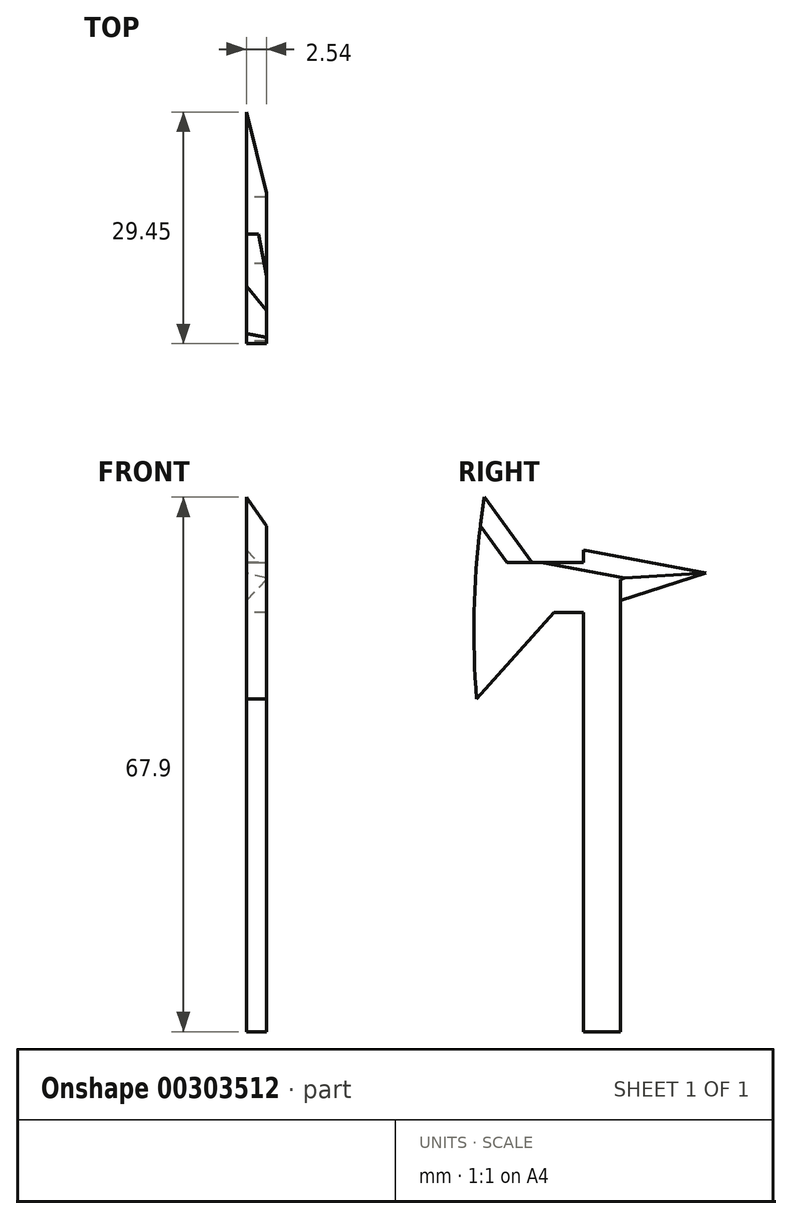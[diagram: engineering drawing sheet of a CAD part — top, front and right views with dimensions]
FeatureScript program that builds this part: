
annotation { "Feature Type Name" : "Feature", "Feature Type Description" : "" }
export const myFeature = defineFeature(function(context is Context, id is Id, definition is map)
    precondition{}
    {
        {
            var Q0;
            Q0=qCreatedBy(makeId("Right.planeOp"),FACE);
            var sketch = newSketch(context, id + "F0", { "sketchPlane" : qUnion([Q0])});
            skLineSegment(sketch, "E0", {"start": v(-4.7, 0) * mm, "end": v(-4.7, -62.89) * mm});
            skLineSegment(sketch, "E1", {"start": v(-4.7, -62.89) * mm, "end": v(0, -62.89) * mm});
            skLineSegment(sketch, "E2", {"start": v(-4.7, 0) * mm, "end": v(0, 0) * mm});
            skPoint(sketch, "E3.endSnap0", {"position": v(-2.35, 0) * mm});
            skLineSegment(sketch, "E4", {"start": v(0, 0) * mm, "end": v(21.16, -4) * mm});
            skLineSegment(sketch, "E5", {"start": v(0, -10.77) * mm, "end": v(21.16, -4) * mm});
            skLineSegment(sketch, "E6", {"start": v(-4.7, -3.27) * mm, "end": v(-8.13, -3.27) * mm});
            skLineSegment(sketch, "E7", {"start": v(-8.13, -3.27) * mm, "end": v(-16.72, 8.5) * mm});
            skLineSegment(sketch, "E8", {"start": v(-18.28, -20.64) * mm, "end": v(-8.44, -9.64) * mm});
            skLineSegment(sketch, "E9", {"start": v(-8.44, -9.64) * mm, "end": v(-4.7, -9.64) * mm});
            skArc(sketch, "E10", {"start": v(-16.72, 8.5) * mm, "mid": v(-18.45, -6.02) * mm, "end": v(-18.28, -20.64) * mm});
            skLineSegment(sketch, "E11", {"start": v(-0.3, 0) * mm, "end": v(0, -10.77) * mm});
            skLineSegment(sketch, "E12", {"start": v(0, -10.77) * mm, "end": v(0, -62.89) * mm});
            skSolve(sketch);
        }
        {
            var Q0;
            Q0 = qSketchRegion(id + "F0", true);
            extrude(context, id + "F1", {"entities" : qUnion([Q0]), "depth" : 2.54 * mm});
        }
        {
            var Q0;
            Q0=makeQuery(id+"F1.opExtrude","CAP_EDGE",EDGE,{"disambiguationData":[OSD([sQuery(id+"F0.wireOp",EDGE,"E7")])],"isStart":false});
            chamfer(context, id + "F2", {"entities" : qUnion([Q0]), "width" : 5.08 * mm, "tangentPropagation" : true});
        }
        {
            var Q0;
            Q0=makeQuery(id+"F1.opExtrude","CAP_EDGE",EDGE,{"disambiguationData":[OSD([sQuery(id+"F0.wireOp",EDGE,"E5")])],"isStart":false});
            chamfer(context, id + "F3", {"entities" : qUnion([Q0]), "width" : 5.08 * mm, "tangentPropagation" : true});
        }
        {
            var Q0;
            Q0=makeQuery(id+"F1.opExtrude","CAP_EDGE",EDGE,{"disambiguationData":[OSD([sQuery(id+"F0.wireOp",EDGE,"E4")])],"isStart":false});
            chamfer(context, id + "F4", {"entities" : qUnion([Q0]), "width" : 5.08 * mm, "tangentPropagation" : true});
        }
    });
